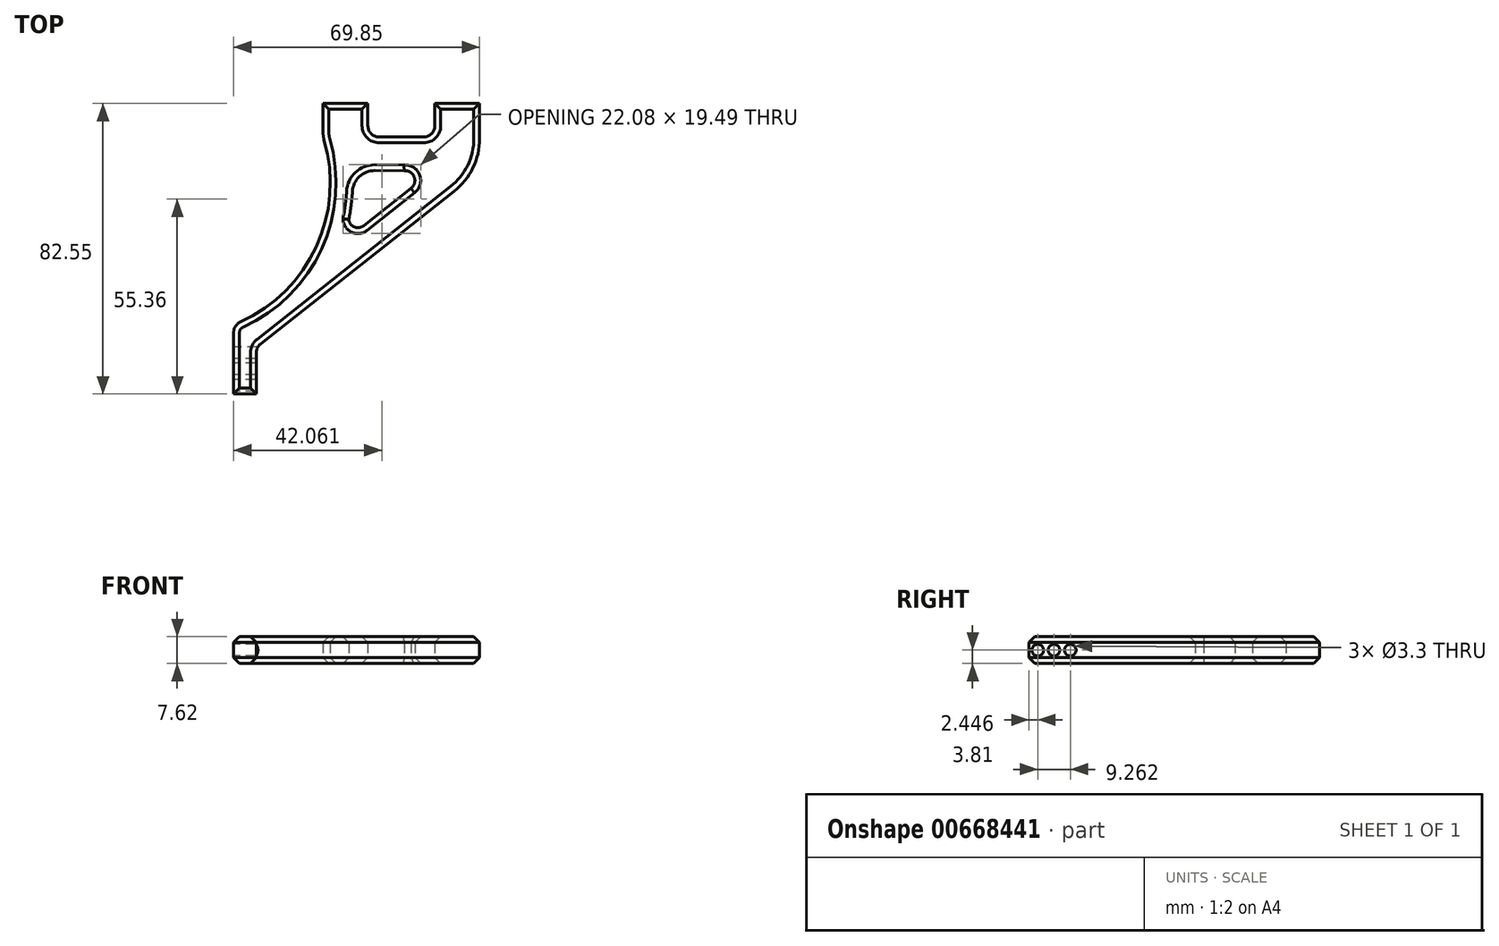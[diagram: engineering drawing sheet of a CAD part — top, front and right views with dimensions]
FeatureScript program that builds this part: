
annotation { "Feature Type Name" : "Feature", "Feature Type Description" : "" }
export const myFeature = defineFeature(function(context is Context, id is Id, definition is map)
    precondition{}
    {
        {
            var Q0;
            Q0=qCreatedBy(makeId("Top.planeOp"),FACE);
            var sketch = newSketch(context, id + "F0", { "sketchPlane" : qUnion([Q0])});
            skLineSegment(sketch, "E0", {"start": v(-21, 29.8) * mm, "end": v(-8.3, 29.8) * mm});
            skPoint(sketch, "E1", {"position": v(-21, -52.76) * mm});
            skPoint(sketch, "E2", {"position": v(-46.4, -52.76) * mm});
            skLineSegment(sketch, "E3", {"start": v(-46.4, -52.76) * mm, "end": v(-46.4, -39.5) * mm});
            skLineSegment(sketch, "E4", {"start": v(-39.96, -41.03) * mm, "end": v(-39.96, -52.76) * mm});
            skLineSegment(sketch, "E5", {"start": v(-39.96, -52.76) * mm, "end": v(-46.4, -52.76) * mm});
            skLineSegment(sketch, "E6", {"start": v(23.46, 29.8) * mm, "end": v(23.46, 19.78) * mm});
            skLineSegment(sketch, "E7", {"start": v(16.2, 4.83) * mm, "end": v(-38.75, -38.54) * mm});
            skLineSegment(sketch, "E8", {"start": v(-46.4, -39.5) * mm, "end": v(-46.4, -35.25) * mm});
            skLineSegment(sketch, "E9", {"start": v(-21, 29.8) * mm, "end": v(-21, 21.2) * mm});
            skArc(sketch, "E10", {"start": v(-44.52, -32.35) * mm, "mid": v(-22.95, -10.92) * mm, "end": v(-20.74, 19.42) * mm});
            skPoint(sketch, "E11", {"position": v(-8.3, 29.8) * mm});
            skPoint(sketch, "E12", {"position": v(10.76, 29.8) * mm});
            skPoint(sketch, "E13", {"position": v(-8.3, 20.27) * mm});
            skLineSegment(sketch, "E14", {"start": v(-8.3, 29.8) * mm, "end": v(-8.3, 23.44) * mm});
            skLineSegment(sketch, "E15", {"start": v(10.76, 23.44) * mm, "end": v(10.76, 29.8) * mm});
            skLineSegment(sketch, "E16", {"start": v(7.58, 20.27) * mm, "end": v(-5.12, 20.27) * mm});
            skArc(sketch, "E17.0", {"start": v(-13.71, -3.11) * mm, "mid": v(-13.05, 0.76) * mm, "end": v(-12.7, 4.67) * mm});
            skPoint(sketch, "E18", {"position": v(13.93, 10.55) * mm});
            skPoint(sketch, "E19", {"position": v(-8.3, 10.74) * mm});
            skPoint(sketch, "E20.end.orphan", {"position": v(-12.76, 10.74) * mm});
            skLineSegment(sketch, "E21", {"start": v(2.62, 10.63) * mm, "end": v(-6.3, 10.7) * mm});
            skLineSegment(sketch, "E22", {"start": v(4.07, 5.78) * mm, "end": v(-9.54, -4.97) * mm});
            skArc(sketch, "E23.filletArc", {"start": v(-6.3, 10.7) * mm, "mid": v(-10.71, 8.96) * mm, "end": v(-12.7, 4.67) * mm});
            skArc(sketch, "E24", {"start": v(3.78, 5.56) * mm, "mid": v(4.91, 8.79) * mm, "end": v(2.04, 10.64) * mm});
            skArc(sketch, "E25", {"start": v(-10.1, -5.3) * mm, "mid": v(-9.99, -5.24) * mm, "end": v(-9.87, -5.16) * mm});
            skLineSegment(sketch, "E26", {"start": v(-9.87, -5.16) * mm, "end": v(-9.54, -4.97) * mm});
            skArc(sketch, "E27", {"start": v(-13.71, -3.11) * mm, "mid": v(-12.19, -5.3) * mm, "end": v(-9.54, -4.97) * mm});
            skPoint(sketch, "E27.startSnap0", {"position": v(-13.62, -2.65) * mm});
            skPoint(sketch, "E28.orphan", {"position": v(-13.7, -3.06) * mm});
            skPoint(sketch, "E29.orphan", {"position": v(-13.7, -2.65) * mm});
            skPoint(sketch, "E30", {"position": v(3.78, 5.56) * mm});
            skPoint(sketch, "E31", {"position": v(2.04, 10.64) * mm});
            skArc(sketch, "E32.filletArc", {"start": v(-8.3, 23.44) * mm, "mid": v(-7.36, 21.2) * mm, "end": v(-5.12, 20.27) * mm});
            skPoint(sketch, "E33.visualSharp", {"position": v(10.76, 20.27) * mm});
            skArc(sketch, "E33.filletArc", {"start": v(7.58, 20.27) * mm, "mid": v(9.83, 21.2) * mm, "end": v(10.76, 23.44) * mm});
            skPoint(sketch, "E34.visualSharp", {"position": v(-39.96, -39.5) * mm});
            skArc(sketch, "E34.filletArc", {"start": v(-38.75, -38.54) * mm, "mid": v(-39.64, -39.65) * mm, "end": v(-39.96, -41.03) * mm});
            skPoint(sketch, "E35.visualSharp", {"position": v(-46.4, -33.14) * mm});
            skArc(sketch, "E35.filletArc", {"start": v(-44.52, -32.35) * mm, "mid": v(-45.88, -33.52) * mm, "end": v(-46.4, -35.25) * mm});
            skPoint(sketch, "E36.visualSharp", {"position": v(23.46, 10.55) * mm});
            skArc(sketch, "E36.filletArc", {"start": v(16.2, 4.83) * mm, "mid": v(21.55, 11.47) * mm, "end": v(23.46, 19.78) * mm});
            skPoint(sketch, "E37.visualSharp", {"position": v(-21, 20.26) * mm});
            skArc(sketch, "E37.filletArc", {"start": v(-21, 21.2) * mm, "mid": v(-20.93, 20.3) * mm, "end": v(-20.74, 19.42) * mm});
            skLineSegment(sketch, "E38.trimOffspring", {"start": v(10.76, 29.8) * mm, "end": v(23.46, 29.8) * mm});
            skSolve(sketch);
        }
        {
            var Q0;
            Q0=makeQuery(id+"F0.imprint","IMPRINT",FACE,{"disambiguationData":[TD([[makeQuery(id+"F0.imprint","IMPRINT",EDGE,{"derivedFrom":sQuery(id+"F0.wireOp",EDGE,"E0")}),-1.0]])]});
            extrude(context, id + "F1", {"entities" : qUnion([Q0]), "depth" : 7.62 * mm});
        }
        {
            var Q0;
            Q0=makeQuery(id+"F1.opExtrude","CAP_FACE",FACE,{"disambiguationData":[OSD([sQuery(id+"F0.wireOp",EDGE,"E0"),sQuery(id+"F0.wireOp",EDGE,"E3"),sQuery(id+"F0.wireOp",EDGE,"E4"),sQuery(id+"F0.wireOp",EDGE,"E5"),sQuery(id+"F0.wireOp",EDGE,"E6"),sQuery(id+"F0.wireOp",EDGE,"E7"),sQuery(id+"F0.wireOp",EDGE,"E8"),sQuery(id+"F0.wireOp",EDGE,"E9"),sQuery(id+"F0.wireOp",EDGE,"E10"),sQuery(id+"F0.wireOp",EDGE,"E14"),sQuery(id+"F0.wireOp",EDGE,"E15"),sQuery(id+"F0.wireOp",EDGE,"E16"),sQuery(id+"F0.wireOp",EDGE,"E17.0"),sQuery(id+"F0.wireOp",EDGE,"E21"),sQuery(id+"F0.wireOp",EDGE,"E22"),sQuery(id+"F0.wireOp",EDGE,"E23.filletArc"),sQuery(id+"F0.wireOp",EDGE,"E24"),sQuery(id+"F0.wireOp",EDGE,"E27"),sQuery(id+"F0.wireOp",EDGE,"E32.filletArc"),sQuery(id+"F0.wireOp",EDGE,"E33.filletArc"),sQuery(id+"F0.wireOp",EDGE,"E34.filletArc"),sQuery(id+"F0.wireOp",EDGE,"E35.filletArc"),sQuery(id+"F0.wireOp",EDGE,"E36.filletArc"),sQuery(id+"F0.wireOp",EDGE,"E37.filletArc"),sQuery(id+"F0.wireOp",EDGE,"E38.trimOffspring")])],"isStart":false});
            var Q1;
            Q1=makeQuery(id+"F1.opExtrude","CAP_FACE",FACE,{"disambiguationData":[OSD([sQuery(id+"F0.wireOp",EDGE,"E0"),sQuery(id+"F0.wireOp",EDGE,"E3"),sQuery(id+"F0.wireOp",EDGE,"E4"),sQuery(id+"F0.wireOp",EDGE,"E5"),sQuery(id+"F0.wireOp",EDGE,"E6"),sQuery(id+"F0.wireOp",EDGE,"E7"),sQuery(id+"F0.wireOp",EDGE,"E8"),sQuery(id+"F0.wireOp",EDGE,"E9"),sQuery(id+"F0.wireOp",EDGE,"E10"),sQuery(id+"F0.wireOp",EDGE,"E14"),sQuery(id+"F0.wireOp",EDGE,"E15"),sQuery(id+"F0.wireOp",EDGE,"E16"),sQuery(id+"F0.wireOp",EDGE,"E17.0"),sQuery(id+"F0.wireOp",EDGE,"E21"),sQuery(id+"F0.wireOp",EDGE,"E22"),sQuery(id+"F0.wireOp",EDGE,"E23.filletArc"),sQuery(id+"F0.wireOp",EDGE,"E24"),sQuery(id+"F0.wireOp",EDGE,"E27"),sQuery(id+"F0.wireOp",EDGE,"E32.filletArc"),sQuery(id+"F0.wireOp",EDGE,"E33.filletArc"),sQuery(id+"F0.wireOp",EDGE,"E34.filletArc"),sQuery(id+"F0.wireOp",EDGE,"E35.filletArc"),sQuery(id+"F0.wireOp",EDGE,"E36.filletArc"),sQuery(id+"F0.wireOp",EDGE,"E37.filletArc"),sQuery(id+"F0.wireOp",EDGE,"E38.trimOffspring")])],"isStart":true});
            chamfer(context, id + "F2", {"entities" : qUnion([Q0, Q1]), "width" : 1.65 * mm, "tangentPropagation" : true});
        }
        {
            var Q0;
            Q0=makeQuery(id+"F1.opExtrude","SWEPT_FACE",FACE,{"disambiguationData":[OSD([sQuery(id+"F0.wireOp",EDGE,"E3"),sQuery(id+"F0.wireOp",EDGE,"E8")])]});
            var sketch = newSketch(context, id + "F3", { "sketchPlane" : qUnion([Q0])});
            skCircle(sketch, "E39", {"center": v(50.31, 3.8) * mm, "radius": 1.45 * mm});
            skCircle(sketch, "E40", {"center": v(41.05, 3.81) * mm, "radius": 1.47 * mm});
            skPoint(sketch, "E41.trimOffspring.end.orphan", {"position": v(35.25, 3.81) * mm});
            skPoint(sketch, "E42.start.orphan", {"position": v(52.76, 3.81) * mm});
            skCircle(sketch, "E43", {"center": v(45.7, 3.81) * mm, "radius": 1.35 * mm});
            skLineSegment(sketch, "E44", {"start": v(35.25, 3.81) * mm, "end": v(52.76, 3.81) * mm});
            skSolve(sketch);
        }
        {
            var Q0;
            Q0=sQuery(id+"F3.wireOp",VERTEX,"E40.center");
            var Q1;
            Q1=sQuery(id+"F3.wireOp",VERTEX,"E43.center");
            var Q2;
            Q2=sQuery(id+"F3.wireOp",VERTEX,"E39.center");
            var Q3;
            Q3=makeQuery(id+"F1.opExtrude","SWEPT_BODY",BODY,{"disambiguationData":[OSD([sQuery(id+"F0.wireOp",EDGE,"E0"),sQuery(id+"F0.wireOp",EDGE,"E3"),sQuery(id+"F0.wireOp",EDGE,"E4"),sQuery(id+"F0.wireOp",EDGE,"E5"),sQuery(id+"F0.wireOp",EDGE,"E6"),sQuery(id+"F0.wireOp",EDGE,"E7"),sQuery(id+"F0.wireOp",EDGE,"E8"),sQuery(id+"F0.wireOp",EDGE,"E9"),sQuery(id+"F0.wireOp",EDGE,"E10"),sQuery(id+"F0.wireOp",EDGE,"E14"),sQuery(id+"F0.wireOp",EDGE,"E15"),sQuery(id+"F0.wireOp",EDGE,"E16"),sQuery(id+"F0.wireOp",EDGE,"E17.0"),sQuery(id+"F0.wireOp",EDGE,"E21"),sQuery(id+"F0.wireOp",EDGE,"E22"),sQuery(id+"F0.wireOp",EDGE,"E23.filletArc"),sQuery(id+"F0.wireOp",EDGE,"E24"),sQuery(id+"F0.wireOp",EDGE,"E27"),sQuery(id+"F0.wireOp",EDGE,"E32.filletArc"),sQuery(id+"F0.wireOp",EDGE,"E33.filletArc"),sQuery(id+"F0.wireOp",EDGE,"E34.filletArc"),sQuery(id+"F0.wireOp",EDGE,"E35.filletArc"),sQuery(id+"F0.wireOp",EDGE,"E36.filletArc"),sQuery(id+"F0.wireOp",EDGE,"E37.filletArc"),sQuery(id+"F0.wireOp",EDGE,"E38.trimOffspring")])]});
            hole(context, id + "F4", {"style" : HoleStyle.SIMPLE, "endStyle" : HoleEndStyle.THROUGH, "standardTappedOrClearance" : lookupTablePath({ "standard" : "ISO", "fit" : "Normal", "size" : "M3", "type" : "Clearance" }), "standardBlindInLast" : lookupTablePath({ "fit" : "Standard", "standard" : "ISO", "size" : "M3", "type" : "Clearance" }), "holeDiameter" : 3.3 * mm, "isTappedThrough" : true, "tappedDepth" : 12.7 * mm, "tapClearance" : 3, "locations" : qUnion([Q0, Q1, Q2]), "scope" : qUnion([Q3])});
        }
    });
